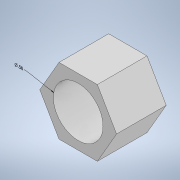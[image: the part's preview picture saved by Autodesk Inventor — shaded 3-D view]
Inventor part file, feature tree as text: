
AUTODESK INVENTOR PART (.ipt)
format: ipt  version: 2021.2 (Build 252289000, 289)  size: 107,520 bytes
history: native  units: in
note: dims shown in document units (in); Inventor stores cm internally (conversion verified against a paired STEP export)
features: other x2, extrude x1, sketch x1
ambient origin geometry x8: Origin, YZ Plane, XZ Plane, XY Plane, X Axis, Y Axis, Z Axis, Center Point
bodies: Solid1 (feature_tree)
feature tree (4):
  other  "Annotations"
  extrude  "Extrusion1"  Depth=0.5in
  sketch  "Sketch1"  dims[d0=0.6693in d1=0.5in d2=0.5in d3=0.0in d4=1.165in d5=0.5in]
  other  "Diameter Dimension 1"
